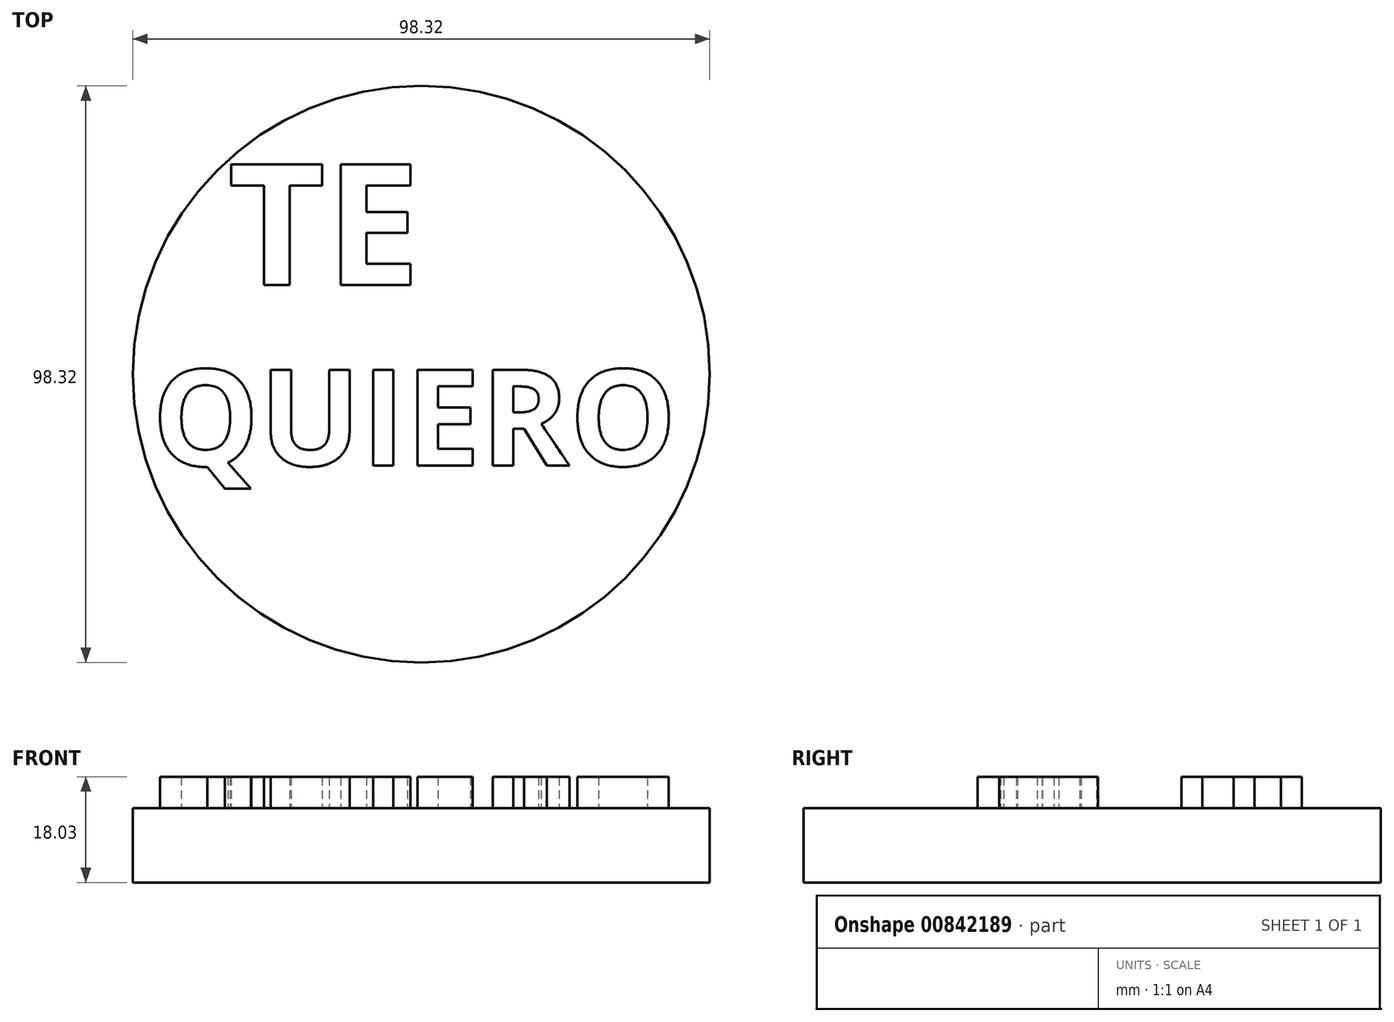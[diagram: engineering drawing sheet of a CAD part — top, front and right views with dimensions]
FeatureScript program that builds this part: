
annotation { "Feature Type Name" : "Feature", "Feature Type Description" : "" }
export const myFeature = defineFeature(function(context is Context, id is Id, definition is map)
    precondition{}
    {
        {
            var Q0;
            Q0=qCreatedBy(makeId("Top.planeOp"),FACE);
            var sketch = newSketch(context, id + "F0", { "sketchPlane" : qUnion([Q0])});
            skCircle(sketch, "E0", {"center": v(0, 0) * mm, "radius": 49.16 * mm});
            skSolve(sketch);
        }
        {
            var Q0;
            Q0=makeQuery(id+"F0.imprint","IMPRINT",FACE,{"disambiguationData":[TD([[makeQuery(id+"F0.imprint","IMPRINT",EDGE,{"derivedFrom":sQuery(id+"F0.wireOp",EDGE,"E0")}),1.0]])]});
            extrude(context, id + "F1", {"entities" : qUnion([Q0]), "depth" : 12.7 * mm, "offsetDistance" : 25.4 * mm});
        }
        {
            var Q0;
            Q0=makeQuery(id+"F1.opExtrude","CAP_FACE",FACE,{"disambiguationData":[OSD([sQuery(id+"F0.wireOp",EDGE,"E0")])],"isStart":false});
            var sketch = newSketch(context, id + "F2", { "sketchPlane" : qUnion([Q0])});
            skText(sketch, "E1", { "text": "TE", "fontName": "OpenSans-Bold.ttf"});
            const initialGuessF2  = {"E1": [-0.03296, 0.0152, 1, 0, 0.02073]};
            skSetInitialGuess(sketch, initialGuessF2);
            skSolve(sketch);
        }
        {
            var Q0;
            Q0 = qSketchRegion(id + "F2", true);
            extrude(context, id + "F3", {"entities" : qUnion([Q0]), "operationType" : NewBodyOperationType.ADD, "depth" : 5.33 * mm, "offsetDistance" : 25.4 * mm});
        }
        {
            var Q0;
            Q0=makeQuery(id+"F1.opExtrude","CAP_FACE",FACE,{"disambiguationData":[OSD([sQuery(id+"F0.wireOp",EDGE,"E0")])],"isStart":false});
            var sketch = newSketch(context, id + "F4", { "sketchPlane" : qUnion([Q0])});
            skText(sketch, "E2", { "text": "QUIERO", "fontName": "OpenSans-Bold.ttf"});
            const initialGuessF4  = {"E2": [-0.04584, -0.01561, 1, 0, 0.0165]};
            skSetInitialGuess(sketch, initialGuessF4);
            skSolve(sketch);
        }
        {
            var Q0;
            Q0 = qSketchRegion(id + "F4", true);
            extrude(context, id + "F5", {"entities" : qUnion([Q0]), "operationType" : NewBodyOperationType.ADD, "depth" : 5.33 * mm, "offsetDistance" : 25.4 * mm});
        }
    });
